# Revit family: UL-10D-DSI-Automatic-Fire-Protective-Smoke-Curtains
name_source: partatom
category: Specialty Equipment
units: mm (PartAtom-declared; Revit-internal decimal feet)

## family parameters
Always vertical = No
Cut with Voids When Loaded = No
Enable Cutting in Views = No
Maintain Annotation Orientation = No
OmniClass Number = 23.30.60.17
OmniClass Title = Fire and Smoke Shutters and Curtains
Part Type = Normal
Room Calculation Point = No
Round Connector Dimension = Use Diameter
Shared = No
Work Plane-Based = Yes

## types (3) — shared parameters
Assembly Code = D4090
CAD Details = https://www.arcat.com
Default Elevation = 0' - 0"
Description = Door Systems Inc Fire Rated Smoke Curtain - as Specified
Electrical_Voltage = 24 V
Fire Performance = Fire Rating as Specified  ;  UL10B and UL 263 Time Curve
Keynote = 08 34 85
Manufacturer = Door Systems, Inc
Maximum Size = 14 ft Wide. Heights Above 10 ft Require Larger Head Clearances
Model = as Specified
Product Page URL = https://www.arcat.com
Specification = https://www.arcat.com
URL = http://www.doorsysinc.com

## type names
- Multiple Roller Over Under
- Multiple Roller Side by Side
- Single Roller
type visibility flags: 3 boolean params named "<type name>" — each type sets only its own to Yes (folded from table)

## geometry (parser evidence)
native form markers: Sweep x3
no freeform markers — native parametric forms only
